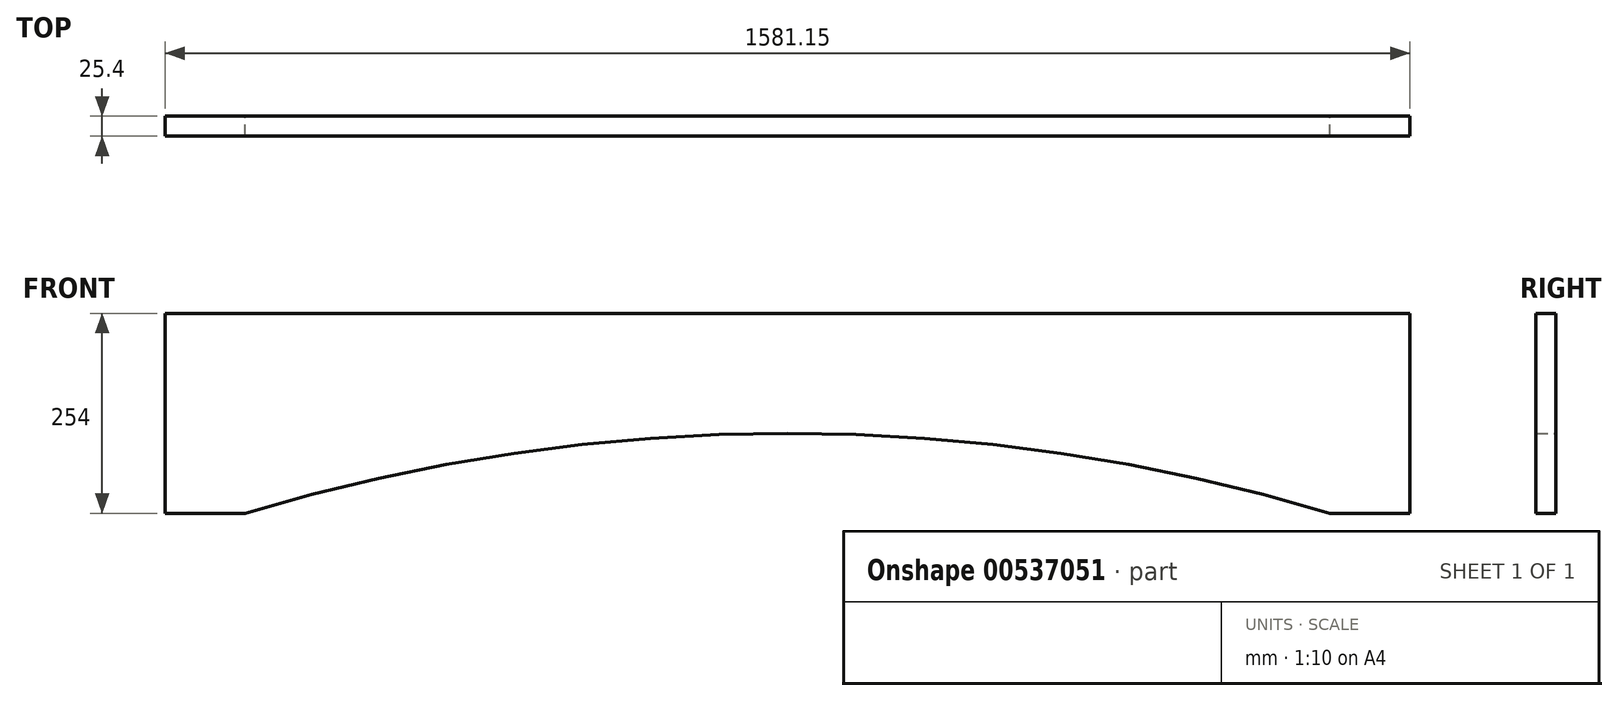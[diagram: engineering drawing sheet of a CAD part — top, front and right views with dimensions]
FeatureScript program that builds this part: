
annotation { "Feature Type Name" : "Feature", "Feature Type Description" : "" }
export const myFeature = defineFeature(function(context is Context, id is Id, definition is map)
    precondition{}
    {
        {
            var Q0;
            Q0=qCreatedBy(makeId("Front.planeOp"),FACE);
            var sketch = newSketch(context, id + "F0", { "sketchPlane" : qUnion([Q0])});
            skLineSegment(sketch, "E0", {"start": v(-88.36, 170.86) * mm, "end": v(1492.79, 170.86) * mm});
            skLineSegment(sketch, "E1", {"start": v(1492.79, 170.86) * mm, "end": v(1492.79, -83.14) * mm});
            skLineSegment(sketch, "E2", {"start": v(-88.36, 170.86) * mm, "end": v(-88.36, -83.14) * mm});
            skLineSegment(sketch, "E3", {"start": v(-88.36, -83.14) * mm, "end": v(13.24, -83.14) * mm});
            skLineSegment(sketch, "E4", {"start": v(1492.79, -83.14) * mm, "end": v(1391.19, -83.14) * mm});
            skArc(sketch, "E5", {"start": v(1391.19, -83.14) * mm, "mid": v(702.21, 18.46) * mm, "end": v(13.24, -83.14) * mm});
            skPoint(sketch, "E6.start.orphan", {"position": v(702.21, 170.86) * mm});
            skSolve(sketch);
        }
        {
            var Q0;
            Q0 = qSketchRegion(id + "F0", true);
            extrude(context, id + "F1", {"entities" : qUnion([Q0]), "depth" : 25.4 * mm, "offsetDistance" : 25.4 * mm});
        }
    });
